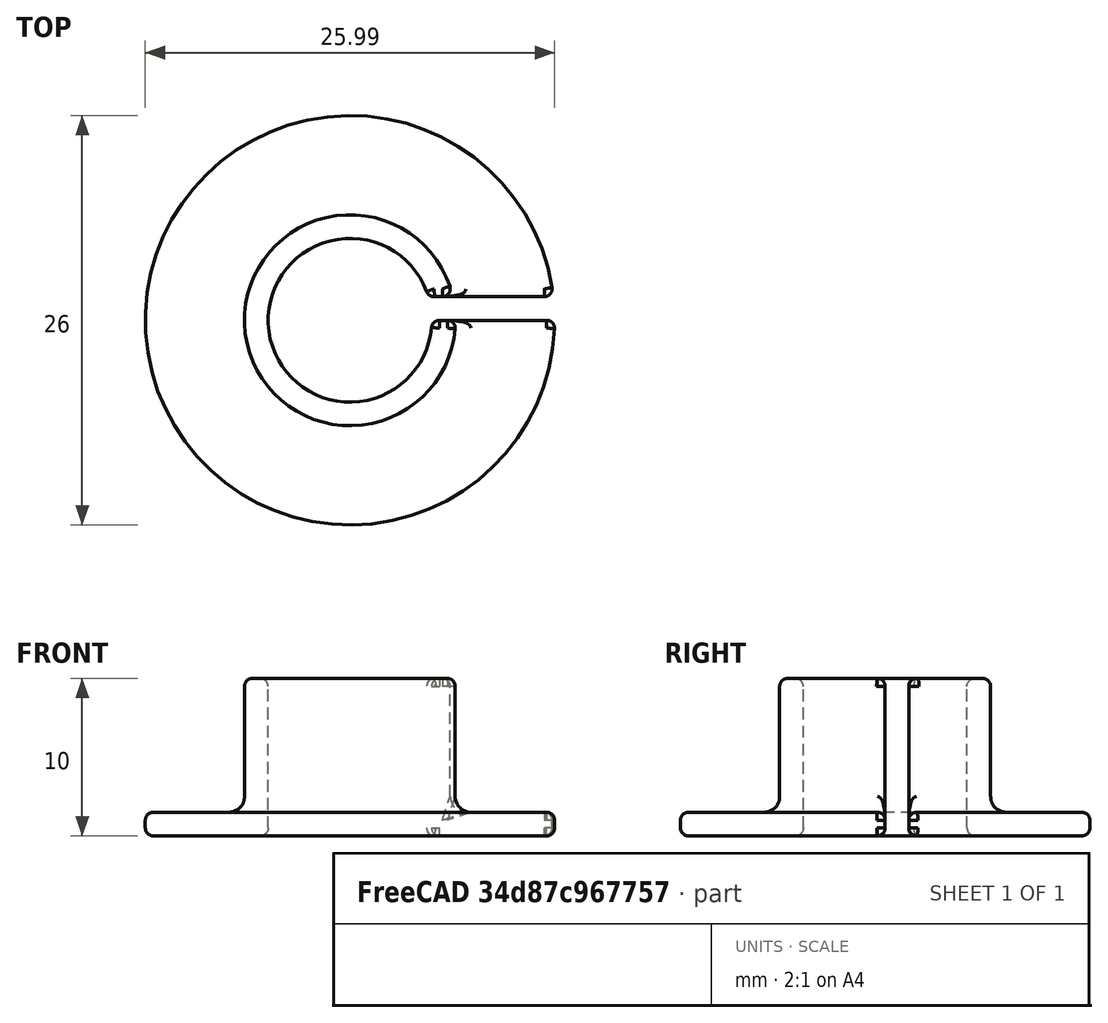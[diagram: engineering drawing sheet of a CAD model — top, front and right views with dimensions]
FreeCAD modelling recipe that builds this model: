
FCSTD DOCUMENT  (FreeCAD 0.16R6712 (Git))
Label: PenCollar
License: All rights reserved
LicenseURL: http://en.wikipedia.org/wiki/All_rights_reserved
objects: PartDesign::Fillet×7, Part::Cylinder×3, Part::MultiFuse×2, Sketcher::SketchObject×1, Spreadsheet::Sheet×1, Part::Box×1, Part::Cut×1
note: 15 computed .brp shape members not serialized (recipe doc carries the construction recipe); baked Part::Feature solids carry a one-line shape summary decoded from their .brp

FEATURE [Sketcher::SketchObject] Sketch
FEATURE [Part::Cylinder] Cylinder  label="hatBase"
  Angle = 360
  Height = 1.5
  Radius = 13
  expr: Height = data.wallWidth
  expr: Radius = data.hatDiameter / 2
FEATURE [Part::Cylinder] Cylinder001  label="hatBody"
  Angle = 360
  Height = 10
  Radius = 6.7
  expr: Radius = data.penDiameter / 2 + data.wallWidth
  expr: Height = data.hatHeight
FEATURE [Spreadsheet::Sheet] Spreadsheet  label="data"
  cells = A3=penDiameter; B3(penDiameter)==10.4mm; A4=penRadius; B4==data.penDiameter / 2; A5=wallWidth; B5(wallWidth)==1.5mm; A6=hatDiameter; B6(hatDiameter)==26mm; A7=hatRadius; B7==data.hatDiameter / 2; A8=hatHeight; B8(hatHeight)==10mm
FEATURE [Part::Cylinder] Cylinder002  label="bore"
  Angle = 360
  Height = 11
  Radius = 5.2
  expr: Height = data.hatHeight + 1mm
  expr: Radius = data.penDiameter / 2
FEATURE [Part::Box] Box  label="slice"
  Height = 10
  Length = 13
  Width = 1.5
  expr: Length = data.hatDiameter / 2
  expr: Width = data.wallWidth
FEATURE [Part::MultiFuse] Fusion  label="body"
  Shapes = -> [Cylinder,Cylinder001]
FEATURE [Part::MultiFuse] Fusion001  label="cut"
  Shapes = -> [Box,Cylinder002]
FEATURE [Part::Cut] Cut
  Base = -> Fusion
  Tool = -> Fusion001
FEATURE [PartDesign::Fillet] Fillet
  Base = -> Cut [Edge21,Edge19]
  Radius = 0.5
FEATURE [PartDesign::Fillet] Fillet001
  Base = -> Fillet [Edge20]
  Radius = 0.5
FEATURE [PartDesign::Fillet] Fillet002
  Base = -> Fillet001 [Edge12]
  Radius = 0.5
FEATURE [PartDesign::Fillet] Fillet003
  Base = -> Fillet002 [Edge26]
  Radius = 0.5
FEATURE [PartDesign::Fillet] Fillet004
  Base = -> Fillet003 [Edge13]
  Radius = 0.5
FEATURE [PartDesign::Fillet] Fillet005
  Base = -> Fillet004 [Edge3]
  Radius = 0.5
FEATURE [PartDesign::Fillet] Fillet006
  Base = -> Fillet005 [Edge4]
  Radius = 1
